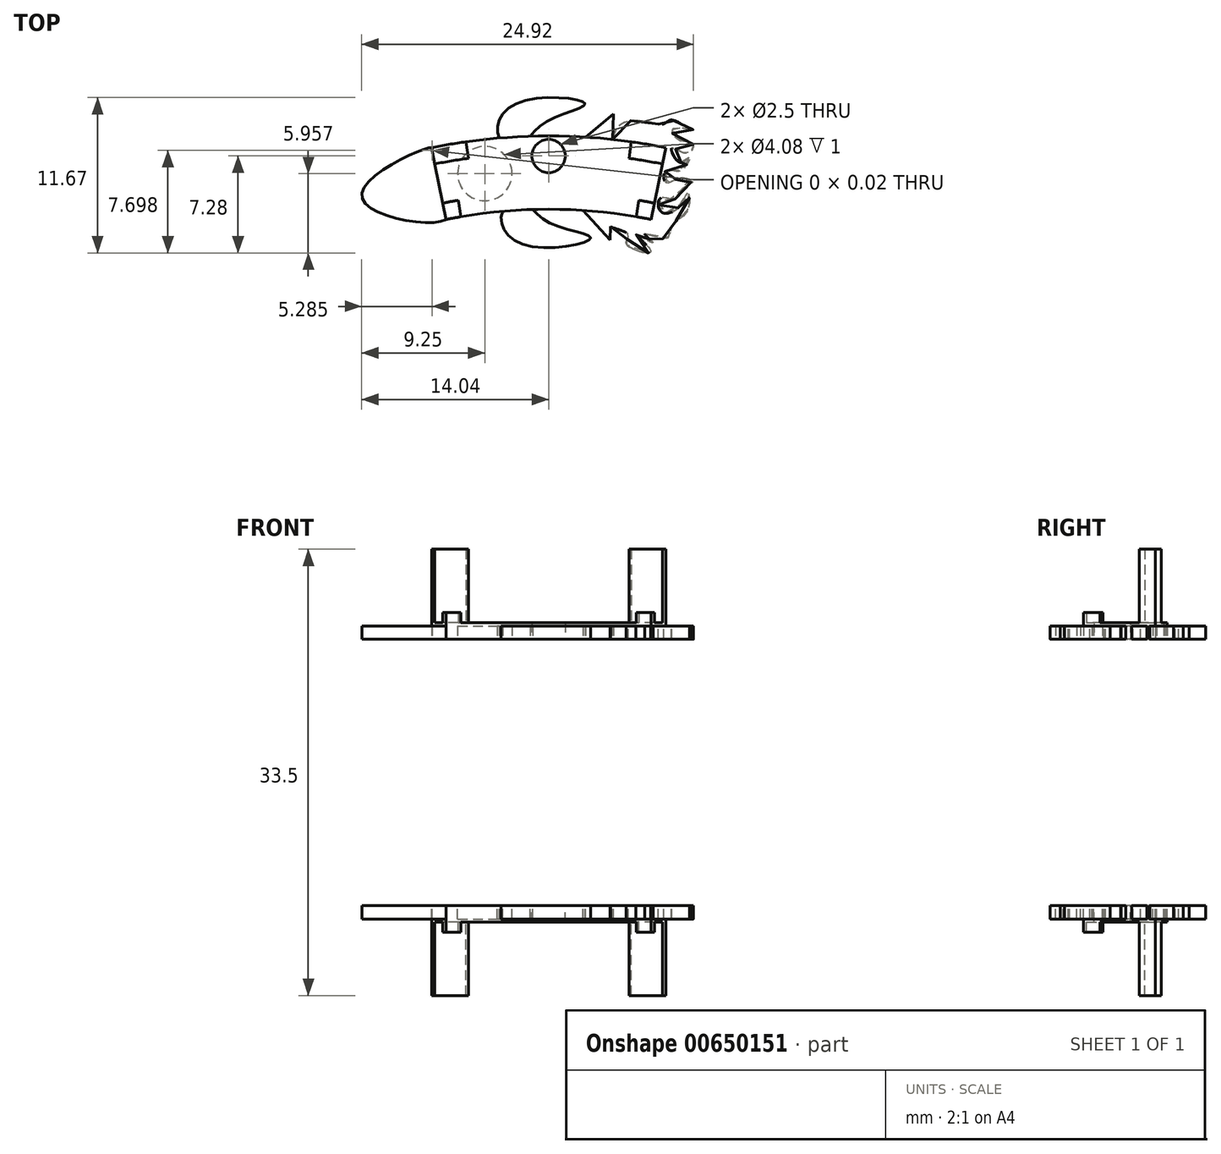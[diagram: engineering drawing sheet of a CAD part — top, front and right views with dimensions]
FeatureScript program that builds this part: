
annotation { "Feature Type Name" : "Feature", "Feature Type Description" : "" }
export const myFeature = defineFeature(function(context is Context, id is Id, definition is map)
    precondition{}
    {
        {
            var Q0;
            Q0=qCreatedBy(makeId("Top.planeOp"),FACE);
            var sketch = newSketch(context, id + "F0", { "sketchPlane" : qUnion([Q0])});
            skCircle(sketch, "E0", {"center": v(0, 0) * mm, "radius": 39 * mm});
            skCircle(sketch, "E1", {"center": v(0, 0) * mm, "radius": 44.5 * mm});
            skCircle(sketch, "E2", {"center": v(0, 43) * mm, "radius": 1.25 * mm});
            skCircle(sketch, "E3", {"center": v(0, 43) * mm, "radius": 6 * mm});
            skLineSegment(sketch, "E4", {"start": v(-7.7, 38.23) * mm, "end": v(-8.8, 43.62) * mm});
            skLineSegment(sketch, "E5", {"start": v(7.7, 38.23) * mm, "end": v(8.8, 43.62) * mm});
            skLineSegment(sketch, "E6", {"start": v(-7.5, 43.86) * mm, "end": v(-6.58, 38.44) * mm});
            skLineSegment(sketch, "E7", {"start": v(6.58, 38.44) * mm, "end": v(7.5, 43.86) * mm});
            skCircle(sketch, "E8", {"center": v(0, 0) * mm, "radius": 40.25 * mm});
            skCircle(sketch, "E9", {"center": v(0, 0) * mm, "radius": 43.25 * mm});
            skSolve(sketch);
        }
        {
            var Q0;
            {var subQ0=sQuery(id+"F0.wireOp",EDGE,"E7");var subQ1=sQuery(id+"F0.wireOp",EDGE,"E1");var subQ2=makeQuery(id+"F0.imprint","INTERSECT",VERTEX,{"derivedFrom":[subQ1,subQ0]});Q0=makeQuery(id+"F0.imprint","IMPRINT",FACE,{"disambiguationData":[TD([[makeQuery(id+"F0.imprint","IMPRINT",EDGE,{"disambiguationData":[TD([[subQ2,-1.0]])],"derivedFrom":subQ1}),1.0]])]});}
            var Q1;
            {var subQ0=sQuery(id+"F0.wireOp",EDGE,"E6");var subQ1=sQuery(id+"F0.wireOp",EDGE,"E1");var subQ2=makeQuery(id+"F0.imprint","INTERSECT",VERTEX,{"derivedFrom":[subQ1,subQ0]});Q1=makeQuery(id+"F0.imprint","IMPRINT",FACE,{"disambiguationData":[TD([[makeQuery(id+"F0.imprint","IMPRINT",EDGE,{"disambiguationData":[TD([[subQ2,1.0]])],"derivedFrom":subQ1}),1.0]])]});}
            var Q2;
            {var subQ0=sQuery(id+"F0.wireOp",EDGE,"E3");var subQ1=sQuery(id+"F0.wireOp",EDGE,"E1");var subQ2=makeQuery(id+"F0.imprint","INTERSECT",VERTEX,{"disambiguationData":[OD(0.0)],"derivedFrom":[subQ1,subQ0]});Q2=makeQuery(id+"F0.imprint","IMPRINT",FACE,{"disambiguationData":[TD([[makeQuery(id+"F0.imprint","IMPRINT",EDGE,{"disambiguationData":[TD([[subQ2,-1.0]])],"derivedFrom":subQ1}),1.0]])]});}
            var Q3;
            {var subQ0=sQuery(id+"F0.wireOp",EDGE,"E8");var subQ1=sQuery(id+"F0.wireOp",EDGE,"E3");var subQ2=makeQuery(id+"F0.imprint","INTERSECT",VERTEX,{"disambiguationData":[OD(1.0)],"derivedFrom":[subQ1,subQ0]});Q3=makeQuery(id+"F0.imprint","IMPRINT",FACE,{"disambiguationData":[TD([[makeQuery(id+"F0.imprint","IMPRINT",EDGE,{"disambiguationData":[TD([[subQ2,-1.0]])],"derivedFrom":subQ1}),-1.0]])]});}
            var Q4;
            {var subQ3=sQuery(id+"F0.wireOp",EDGE,"E9");var subQ5=sQuery(id+"F0.wireOp",EDGE,"E2");var subQ6=makeQuery(id+"F0.imprint","INTERSECT",VERTEX,{"disambiguationData":[OD(0.0)],"derivedFrom":[subQ5,subQ3]});Q4=makeQuery(id+"F0.imprint","IMPRINT",FACE,{"disambiguationData":[TD([[makeQuery(id+"F0.imprint","IMPRINT",EDGE,{"disambiguationData":[TD([[subQ6,1.0]])],"derivedFrom":subQ5}),-1.0]])]});}
            var Q5;
            {var subQ0=sQuery(id+"F0.wireOp",EDGE,"E9");var subQ1=sQuery(id+"F0.wireOp",EDGE,"E3");var subQ2=makeQuery(id+"F0.imprint","INTERSECT",VERTEX,{"disambiguationData":[OD(0.0)],"derivedFrom":[subQ1,subQ0]});Q5=makeQuery(id+"F0.imprint","IMPRINT",FACE,{"disambiguationData":[TD([[makeQuery(id+"F0.imprint","IMPRINT",EDGE,{"disambiguationData":[TD([[subQ2,-1.0]])],"derivedFrom":subQ1}),-1.0]])]});}
            var Q6;
            {var subQ0=sQuery(id+"F0.wireOp",EDGE,"E6");var subQ1=sQuery(id+"F0.wireOp",EDGE,"E0");var subQ2=makeQuery(id+"F0.imprint","INTERSECT",VERTEX,{"derivedFrom":[subQ1,subQ0]});Q6=makeQuery(id+"F0.imprint","IMPRINT",FACE,{"disambiguationData":[TD([[makeQuery(id+"F0.imprint","IMPRINT",EDGE,{"disambiguationData":[TD([[subQ2,1.0]])],"derivedFrom":subQ1}),-1.0]])]});}
            var Q7;
            {var subQ0=sQuery(id+"F0.wireOp",EDGE,"E3");var subQ1=sQuery(id+"F0.wireOp",EDGE,"E0");var subQ2=makeQuery(id+"F0.imprint","INTERSECT",VERTEX,{"disambiguationData":[OD(0.0)],"derivedFrom":[subQ1,subQ0]});Q7=makeQuery(id+"F0.imprint","IMPRINT",FACE,{"disambiguationData":[TD([[makeQuery(id+"F0.imprint","IMPRINT",EDGE,{"disambiguationData":[TD([[subQ2,-1.0]])],"derivedFrom":subQ1}),-1.0]])]});}
            var Q8;
            {var subQ0=sQuery(id+"F0.wireOp",EDGE,"E7");var subQ1=sQuery(id+"F0.wireOp",EDGE,"E0");var subQ2=makeQuery(id+"F0.imprint","INTERSECT",VERTEX,{"derivedFrom":[subQ1,subQ0]});Q8=makeQuery(id+"F0.imprint","IMPRINT",FACE,{"disambiguationData":[TD([[makeQuery(id+"F0.imprint","IMPRINT",EDGE,{"disambiguationData":[TD([[subQ2,-1.0]])],"derivedFrom":subQ1}),-1.0]])]});}
            var Q9;
            {var subQ0=sQuery(id+"F0.wireOp",EDGE,"E8");var subQ1=sQuery(id+"F0.wireOp",EDGE,"E5");var subQ2=makeQuery(id+"F0.imprint","INTERSECT",VERTEX,{"derivedFrom":[subQ1,subQ0]});Q9=makeQuery(id+"F0.imprint","IMPRINT",FACE,{"disambiguationData":[TD([[makeQuery(id+"F0.imprint","IMPRINT",EDGE,{"disambiguationData":[TD([[subQ2,-1.0]])],"derivedFrom":subQ1}),1.0]])]});}
            var Q10;
            {var subQ0=sQuery(id+"F0.wireOp",EDGE,"E8");var subQ1=sQuery(id+"F0.wireOp",EDGE,"E4");var subQ2=makeQuery(id+"F0.imprint","INTERSECT",VERTEX,{"derivedFrom":[subQ1,subQ0]});Q10=makeQuery(id+"F0.imprint","IMPRINT",FACE,{"disambiguationData":[TD([[makeQuery(id+"F0.imprint","IMPRINT",EDGE,{"disambiguationData":[TD([[subQ2,-1.0]])],"derivedFrom":subQ1}),-1.0]])]});}
            extrude(context, id + "F1", {"entities" : qUnion([Q0, Q1, Q2, Q3, Q4, Q5, Q6, Q7, Q8, Q9, Q10]), "depth" : 1.25 * mm, "offsetDistance" : 25 * mm});
        }
        {
            var Q0;
            Q0=qCreatedBy(makeId("Top.planeOp"),FACE);
            var sketch = newSketch(context, id + "F2", { "sketchPlane" : qUnion([Q0])});
            skCircle(sketch, "E10", {"center": v(0, 0) * mm, "radius": 39 * mm});
            skCircle(sketch, "E11", {"center": v(0, 0) * mm, "radius": 44.5 * mm});
            skCircle(sketch, "E12", {"center": v(0, 43) * mm, "radius": 0.85 * mm});
            skCircle(sketch, "E13", {"center": v(0, 43) * mm, "radius": 6 * mm});
            skLineSegment(sketch, "E14", {"start": v(-7.7, 38.23) * mm, "end": v(-8.8, 43.62) * mm});
            skLineSegment(sketch, "E15", {"start": v(7.7, 38.23) * mm, "end": v(8.8, 43.62) * mm});
            skLineSegment(sketch, "E16", {"start": v(-6.2, 44.06) * mm, "end": v(-5.44, 38.62) * mm});
            skLineSegment(sketch, "E17", {"start": v(5.44, 38.62) * mm, "end": v(6.2, 44.06) * mm});
            skCircle(sketch, "E18", {"center": v(0, 0) * mm, "radius": 40.25 * mm});
            skCircle(sketch, "E19", {"center": v(0, 0) * mm, "radius": 43.25 * mm});
            skSolve(sketch);
        }
        {
            var Q0;
            {var subQ0=sQuery(id+"F2.wireOp",EDGE,"E15");var subQ1=sQuery(id+"F2.wireOp",EDGE,"E11");var subQ2=makeQuery(id+"F2.imprint","INTERSECT",VERTEX,{"derivedFrom":[subQ1,subQ0]});Q0=makeQuery(id+"F2.imprint","IMPRINT",FACE,{"disambiguationData":[TD([[makeQuery(id+"F2.imprint","IMPRINT",EDGE,{"disambiguationData":[TD([[subQ2,-1.0]])],"derivedFrom":subQ1}),1.0]])]});}
            var Q1;
            {var subQ0=sQuery(id+"F2.wireOp",EDGE,"E14");var subQ1=sQuery(id+"F2.wireOp",EDGE,"E11");var subQ2=makeQuery(id+"F2.imprint","INTERSECT",VERTEX,{"derivedFrom":[subQ1,subQ0]});Q1=makeQuery(id+"F2.imprint","IMPRINT",FACE,{"disambiguationData":[TD([[makeQuery(id+"F2.imprint","IMPRINT",EDGE,{"disambiguationData":[TD([[subQ2,1.0]])],"derivedFrom":subQ1}),1.0]])]});}
            extrude(context, id + "F3", {"entities" : qUnion([Q0, Q1]), "operationType" : NewBodyOperationType.ADD, "depth" : 6.75 * mm, "offsetDistance" : 25 * mm});
        }
        {
            var Q0;
            Q0=qCreatedBy(makeId("Top.planeOp"),FACE);
            var sketch = newSketch(context, id + "F4", { "sketchPlane" : qUnion([Q0])});
            skCircle(sketch, "E20", {"center": v(0, 0) * mm, "radius": 39 * mm});
            skCircle(sketch, "E21", {"center": v(0, 0) * mm, "radius": 44.5 * mm});
            skCircle(sketch, "E22", {"center": v(0, 43) * mm, "radius": 0.85 * mm});
            skCircle(sketch, "E23", {"center": v(0, 43) * mm, "radius": 6 * mm});
            skLineSegment(sketch, "E24", {"start": v(-7.7, 38.23) * mm, "end": v(-8.8, 43.62) * mm});
            skLineSegment(sketch, "E25", {"start": v(7.7, 38.23) * mm, "end": v(8.8, 43.62) * mm});
            skLineSegment(sketch, "E26", {"start": v(-7.5, 43.86) * mm, "end": v(-6.58, 38.44) * mm});
            skLineSegment(sketch, "E27", {"start": v(6.58, 38.44) * mm, "end": v(7.5, 43.86) * mm});
            skCircle(sketch, "E28", {"center": v(0, 0) * mm, "radius": 40.25 * mm});
            skCircle(sketch, "E29", {"center": v(0, 0) * mm, "radius": 43.25 * mm});
            skSolve(sketch);
        }
        {
            var Q0;
            {var subQ0=sQuery(id+"F4.wireOp",EDGE,"E24");var subQ1=sQuery(id+"F4.wireOp",EDGE,"E20");var subQ2=makeQuery(id+"F4.imprint","INTERSECT",VERTEX,{"derivedFrom":[subQ1,subQ0]});Q0=makeQuery(id+"F4.imprint","IMPRINT",FACE,{"disambiguationData":[TD([[makeQuery(id+"F4.imprint","IMPRINT",EDGE,{"disambiguationData":[TD([[subQ2,1.0]])],"derivedFrom":subQ1}),-1.0]])]});}
            var Q1;
            {var subQ0=sQuery(id+"F4.wireOp",EDGE,"E25");var subQ1=sQuery(id+"F4.wireOp",EDGE,"E20");var subQ2=makeQuery(id+"F4.imprint","INTERSECT",VERTEX,{"derivedFrom":[subQ1,subQ0]});Q1=makeQuery(id+"F4.imprint","IMPRINT",FACE,{"disambiguationData":[TD([[makeQuery(id+"F4.imprint","IMPRINT",EDGE,{"disambiguationData":[TD([[subQ2,-1.0]])],"derivedFrom":subQ1}),-1.0]])]});}
            extrude(context, id + "F5", {"entities" : qUnion([Q0, Q1]), "operationType" : NewBodyOperationType.ADD, "depth" : 2 * mm, "offsetDistance" : 25 * mm});
        }
        {
            var Q0;
            {var subQ0=sQuery(id+"F4.wireOp",EDGE,"E28");var subQ1=sQuery(id+"F4.wireOp",EDGE,"E20");var subQ2=sQuery(id+"F2.wireOp",EDGE,"E19");var subQ3=sQuery(id+"F2.wireOp",EDGE,"E11");Q0=makeQuery(id+"F5.boolean.opBoolean","MERGE",FACE,{"derivedFrom":[makeQuery(id+"F3.boolean.opBoolean","MERGE",FACE,{"derivedFrom":[makeQuery(id+"F1.opExtrude","CAP_FACE",FACE,{"disambiguationData":[OSD([sQuery(id+"F0.wireOp",EDGE,"E0"),sQuery(id+"F0.wireOp",EDGE,"E1"),sQuery(id+"F0.wireOp",EDGE,"E2"),sQuery(id+"F0.wireOp",EDGE,"E4"),sQuery(id+"F0.wireOp",EDGE,"E5"),sQuery(id+"F0.wireOp",EDGE,"E6"),sQuery(id+"F0.wireOp",EDGE,"E7"),sQuery(id+"F0.wireOp",EDGE,"E8"),sQuery(id+"F0.wireOp",EDGE,"E9")])],"isStart":true}),makeQuery(id+"F3.opExtrude","CAP_FACE",FACE,{"disambiguationData":[OSD([subQ3,sQuery(id+"F2.wireOp",EDGE,"E15"),sQuery(id+"F2.wireOp",EDGE,"E17"),subQ2])],"isStart":true}),makeQuery(id+"F3.opExtrude","CAP_FACE",FACE,{"disambiguationData":[OSD([subQ3,sQuery(id+"F2.wireOp",EDGE,"E14"),sQuery(id+"F2.wireOp",EDGE,"E16"),subQ2])],"isStart":true})]}),makeQuery(id+"F5.opExtrude","CAP_FACE",FACE,{"disambiguationData":[OSD([subQ1,sQuery(id+"F4.wireOp",EDGE,"E25"),sQuery(id+"F4.wireOp",EDGE,"E27"),subQ0])],"isStart":true}),makeQuery(id+"F5.opExtrude","CAP_FACE",FACE,{"disambiguationData":[OSD([subQ1,sQuery(id+"F4.wireOp",EDGE,"E24"),sQuery(id+"F4.wireOp",EDGE,"E26"),subQ0])],"isStart":true})]});}
            var sketch = newSketch(context, id + "F6", { "sketchPlane" : qUnion([Q0])});
            skFitSpline(sketch, "E30", {"points": [v(-8.8, -43.62) * mm, v(-14.04, -40.05) * mm, v(-7.7, -38.23) * mm, v(-7.7, -39.96) * mm, v(-8, -41.27) * mm, v(-8.21, -42.6) * mm, v(-8.43, -43.18) * mm, v(-8.75, -43.41) * mm, v(-8.8, -43.62) * mm]});
            skSolve(sketch);
        }
        {
            var Q0;
            Q0=qSketchRegion(id+"F6",true);
            extrude(context, id + "F7", {"entities" : qUnion([Q0]), "operationType" : NewBodyOperationType.ADD, "oppositeDirection" : true, "depth" : 1 * mm, "offsetDistance" : 25 * mm});
        }
        {
            var Q0;
            {var subQ0=sQuery(id+"F4.wireOp",EDGE,"E28");var subQ1=sQuery(id+"F4.wireOp",EDGE,"E20");var subQ2=sQuery(id+"F2.wireOp",EDGE,"E19");var subQ3=sQuery(id+"F2.wireOp",EDGE,"E11");Q0=makeQuery(id+"F7.boolean.opBoolean","MERGE",FACE,{"derivedFrom":[makeQuery(id+"F5.boolean.opBoolean","MERGE",FACE,{"derivedFrom":[makeQuery(id+"F3.boolean.opBoolean","MERGE",FACE,{"derivedFrom":[makeQuery(id+"F1.opExtrude","CAP_FACE",FACE,{"disambiguationData":[OSD([sQuery(id+"F0.wireOp",EDGE,"E0"),sQuery(id+"F0.wireOp",EDGE,"E1"),sQuery(id+"F0.wireOp",EDGE,"E2"),sQuery(id+"F0.wireOp",EDGE,"E4"),sQuery(id+"F0.wireOp",EDGE,"E5"),sQuery(id+"F0.wireOp",EDGE,"E6"),sQuery(id+"F0.wireOp",EDGE,"E7"),sQuery(id+"F0.wireOp",EDGE,"E8"),sQuery(id+"F0.wireOp",EDGE,"E9")])],"isStart":true}),makeQuery(id+"F3.opExtrude","CAP_FACE",FACE,{"disambiguationData":[OSD([subQ3,sQuery(id+"F2.wireOp",EDGE,"E15"),sQuery(id+"F2.wireOp",EDGE,"E17"),subQ2])],"isStart":true}),makeQuery(id+"F3.opExtrude","CAP_FACE",FACE,{"disambiguationData":[OSD([subQ3,sQuery(id+"F2.wireOp",EDGE,"E14"),sQuery(id+"F2.wireOp",EDGE,"E16"),subQ2])],"isStart":true})]}),makeQuery(id+"F5.opExtrude","CAP_FACE",FACE,{"disambiguationData":[OSD([subQ1,sQuery(id+"F4.wireOp",EDGE,"E25"),sQuery(id+"F4.wireOp",EDGE,"E27"),subQ0])],"isStart":true}),makeQuery(id+"F5.opExtrude","CAP_FACE",FACE,{"disambiguationData":[OSD([subQ1,sQuery(id+"F4.wireOp",EDGE,"E24"),sQuery(id+"F4.wireOp",EDGE,"E26"),subQ0])],"isStart":true})]}),makeQuery(id+"F7.opExtrude","CAP_FACE",FACE,{"disambiguationData":[OSD([sQuery(id+"F6.wireOp",EDGE,"E30")])],"isStart":true})]});}
            var sketch = newSketch(context, id + "F8", { "sketchPlane" : qUnion([Q0])});
            skCircle(sketch, "E31", {"center": v(-4.8, -41.68) * mm, "radius": 2.04 * mm});
            skSolve(sketch);
        }
        {
            var Q0;
            Q0=qSketchRegion(id+"F8",true);
            extrude(context, id + "F9", {"entities" : qUnion([Q0]), "operationType" : NewBodyOperationType.REMOVE, "oppositeDirection" : true, "depth" : 1 * mm, "offsetDistance" : 25 * mm});
        }
        {
            var Q0;
            {var subQ0=sQuery(id+"F4.wireOp",EDGE,"E28");var subQ1=sQuery(id+"F4.wireOp",EDGE,"E20");var subQ2=sQuery(id+"F2.wireOp",EDGE,"E19");var subQ3=sQuery(id+"F2.wireOp",EDGE,"E11");Q0=makeQuery(id+"F7.boolean.opBoolean","MERGE",FACE,{"derivedFrom":[makeQuery(id+"F5.boolean.opBoolean","MERGE",FACE,{"derivedFrom":[makeQuery(id+"F3.boolean.opBoolean","MERGE",FACE,{"derivedFrom":[makeQuery(id+"F1.opExtrude","CAP_FACE",FACE,{"disambiguationData":[OSD([sQuery(id+"F0.wireOp",EDGE,"E0"),sQuery(id+"F0.wireOp",EDGE,"E1"),sQuery(id+"F0.wireOp",EDGE,"E2"),sQuery(id+"F0.wireOp",EDGE,"E4"),sQuery(id+"F0.wireOp",EDGE,"E5"),sQuery(id+"F0.wireOp",EDGE,"E6"),sQuery(id+"F0.wireOp",EDGE,"E7"),sQuery(id+"F0.wireOp",EDGE,"E8"),sQuery(id+"F0.wireOp",EDGE,"E9")])],"isStart":true}),makeQuery(id+"F3.opExtrude","CAP_FACE",FACE,{"disambiguationData":[OSD([subQ3,sQuery(id+"F2.wireOp",EDGE,"E15"),sQuery(id+"F2.wireOp",EDGE,"E17"),subQ2])],"isStart":true}),makeQuery(id+"F3.opExtrude","CAP_FACE",FACE,{"disambiguationData":[OSD([subQ3,sQuery(id+"F2.wireOp",EDGE,"E14"),sQuery(id+"F2.wireOp",EDGE,"E16"),subQ2])],"isStart":true})]}),makeQuery(id+"F5.opExtrude","CAP_FACE",FACE,{"disambiguationData":[OSD([subQ1,sQuery(id+"F4.wireOp",EDGE,"E25"),sQuery(id+"F4.wireOp",EDGE,"E27"),subQ0])],"isStart":true}),makeQuery(id+"F5.opExtrude","CAP_FACE",FACE,{"disambiguationData":[OSD([subQ1,sQuery(id+"F4.wireOp",EDGE,"E24"),sQuery(id+"F4.wireOp",EDGE,"E26"),subQ0])],"isStart":true})]}),makeQuery(id+"F7.opExtrude","CAP_FACE",FACE,{"disambiguationData":[OSD([sQuery(id+"F6.wireOp",EDGE,"E30")])],"isStart":true})]});}
            var sketch = newSketch(context, id + "F10", { "sketchPlane" : qUnion([Q0])});
            skFitSpline(sketch, "E32", {"points": [v(-2.2, -43.63) * mm, v(-3.7, -44.35) * mm, v(-2.48, -46.91) * mm, v(2.73, -46.92) * mm, v(-0.49, -45.38) * mm, v(-2.2, -43.63) * mm]});
            skLineSegment(sketch, "E33", {"start": v(3.58, -41.9) * mm, "end": v(-9.05, -41.36) * mm});
            skFitSpline(sketch, "E34.MirrorC", {"points": [v(-2.03, -39.69) * mm, v(-3.46, -38.84) * mm, v(-2.03, -36.4) * mm, v(3.16, -36.83) * mm, v(-0.17, -38.1) * mm, v(-2.03, -39.69) * mm]});
            skSolve(sketch);
        }
        {
            var Q0;
            Q0=qSketchRegion(id+"F10",true);
            extrude(context, id + "F11", {"entities" : qUnion([Q0]), "operationType" : NewBodyOperationType.ADD, "oppositeDirection" : true, "depth" : 1 * mm, "offsetDistance" : 25 * mm});
        }
        {
            var Q0;
            {var subQ0=sQuery(id+"F4.wireOp",EDGE,"E28");var subQ1=sQuery(id+"F4.wireOp",EDGE,"E20");var subQ2=sQuery(id+"F2.wireOp",EDGE,"E19");var subQ3=sQuery(id+"F2.wireOp",EDGE,"E11");Q0=makeQuery(id+"F11.boolean.opBoolean","MERGE",FACE,{"derivedFrom":[makeQuery(id+"F7.boolean.opBoolean","MERGE",FACE,{"derivedFrom":[makeQuery(id+"F5.boolean.opBoolean","MERGE",FACE,{"derivedFrom":[makeQuery(id+"F3.boolean.opBoolean","MERGE",FACE,{"derivedFrom":[makeQuery(id+"F1.opExtrude","CAP_FACE",FACE,{"disambiguationData":[OSD([sQuery(id+"F0.wireOp",EDGE,"E0"),sQuery(id+"F0.wireOp",EDGE,"E1"),sQuery(id+"F0.wireOp",EDGE,"E2"),sQuery(id+"F0.wireOp",EDGE,"E4"),sQuery(id+"F0.wireOp",EDGE,"E5"),sQuery(id+"F0.wireOp",EDGE,"E6"),sQuery(id+"F0.wireOp",EDGE,"E7"),sQuery(id+"F0.wireOp",EDGE,"E8"),sQuery(id+"F0.wireOp",EDGE,"E9")])],"isStart":true}),makeQuery(id+"F3.opExtrude","CAP_FACE",FACE,{"disambiguationData":[OSD([subQ3,sQuery(id+"F2.wireOp",EDGE,"E15"),sQuery(id+"F2.wireOp",EDGE,"E17"),subQ2])],"isStart":true}),makeQuery(id+"F3.opExtrude","CAP_FACE",FACE,{"disambiguationData":[OSD([subQ3,sQuery(id+"F2.wireOp",EDGE,"E14"),sQuery(id+"F2.wireOp",EDGE,"E16"),subQ2])],"isStart":true})]}),makeQuery(id+"F5.opExtrude","CAP_FACE",FACE,{"disambiguationData":[OSD([subQ1,sQuery(id+"F4.wireOp",EDGE,"E25"),sQuery(id+"F4.wireOp",EDGE,"E27"),subQ0])],"isStart":true}),makeQuery(id+"F5.opExtrude","CAP_FACE",FACE,{"disambiguationData":[OSD([subQ1,sQuery(id+"F4.wireOp",EDGE,"E24"),sQuery(id+"F4.wireOp",EDGE,"E26"),subQ0])],"isStart":true})]}),makeQuery(id+"F7.opExtrude","CAP_FACE",FACE,{"disambiguationData":[OSD([sQuery(id+"F6.wireOp",EDGE,"E30")])],"isStart":true})]}),makeQuery(id+"F11.opExtrude","CAP_FACE",FACE,{"disambiguationData":[OSD([sQuery(id+"F10.wireOp",EDGE,"E32")])],"isStart":true}),makeQuery(id+"F11.opExtrude","CAP_FACE",FACE,{"disambiguationData":[OSD([sQuery(id+"F10.wireOp",EDGE,"E34.MirrorC")])],"isStart":true})]});}
            var sketch = newSketch(context, id + "F12", { "sketchPlane" : qUnion([Q0])});
            skLineSegment(sketch, "E35", {"start": v(2.76, -44.41) * mm, "end": v(4.86, -46.16) * mm});
            skLineSegment(sketch, "E36", {"start": v(4.86, -46.16) * mm, "end": v(4.62, -36.7) * mm});
            skLineSegment(sketch, "E37", {"start": v(4.62, -36.7) * mm, "end": v(2.6, -38.91) * mm});
            skLineSegment(sketch, "E38", {"start": v(2.6, -38.91) * mm, "end": v(2.76, -44.41) * mm});
            skSolve(sketch);
        }
        {
            var Q0;
            Q0=qSketchRegion(id+"F12",true);
            extrude(context, id + "F13", {"entities" : qUnion([Q0]), "operationType" : NewBodyOperationType.ADD, "oppositeDirection" : true, "depth" : 1 * mm, "offsetDistance" : 25 * mm});
        }
        {
            var Q0;
            {var subQ0=sQuery(id+"F4.wireOp",EDGE,"E28");var subQ1=sQuery(id+"F4.wireOp",EDGE,"E20");var subQ2=sQuery(id+"F2.wireOp",EDGE,"E19");var subQ3=sQuery(id+"F2.wireOp",EDGE,"E11");Q0=makeQuery(id+"F13.boolean.opBoolean","MERGE",FACE,{"derivedFrom":[makeQuery(id+"F11.boolean.opBoolean","MERGE",FACE,{"derivedFrom":[makeQuery(id+"F7.boolean.opBoolean","MERGE",FACE,{"derivedFrom":[makeQuery(id+"F5.boolean.opBoolean","MERGE",FACE,{"derivedFrom":[makeQuery(id+"F3.boolean.opBoolean","MERGE",FACE,{"derivedFrom":[makeQuery(id+"F1.opExtrude","CAP_FACE",FACE,{"disambiguationData":[OSD([sQuery(id+"F0.wireOp",EDGE,"E0"),sQuery(id+"F0.wireOp",EDGE,"E1"),sQuery(id+"F0.wireOp",EDGE,"E2"),sQuery(id+"F0.wireOp",EDGE,"E4"),sQuery(id+"F0.wireOp",EDGE,"E5"),sQuery(id+"F0.wireOp",EDGE,"E6"),sQuery(id+"F0.wireOp",EDGE,"E7"),sQuery(id+"F0.wireOp",EDGE,"E8"),sQuery(id+"F0.wireOp",EDGE,"E9")])],"isStart":true}),makeQuery(id+"F3.opExtrude","CAP_FACE",FACE,{"disambiguationData":[OSD([subQ3,sQuery(id+"F2.wireOp",EDGE,"E15"),sQuery(id+"F2.wireOp",EDGE,"E17"),subQ2])],"isStart":true}),makeQuery(id+"F3.opExtrude","CAP_FACE",FACE,{"disambiguationData":[OSD([subQ3,sQuery(id+"F2.wireOp",EDGE,"E14"),sQuery(id+"F2.wireOp",EDGE,"E16"),subQ2])],"isStart":true})]}),makeQuery(id+"F5.opExtrude","CAP_FACE",FACE,{"disambiguationData":[OSD([subQ1,sQuery(id+"F4.wireOp",EDGE,"E25"),sQuery(id+"F4.wireOp",EDGE,"E27"),subQ0])],"isStart":true}),makeQuery(id+"F5.opExtrude","CAP_FACE",FACE,{"disambiguationData":[OSD([subQ1,sQuery(id+"F4.wireOp",EDGE,"E24"),sQuery(id+"F4.wireOp",EDGE,"E26"),subQ0])],"isStart":true})]}),makeQuery(id+"F7.opExtrude","CAP_FACE",FACE,{"disambiguationData":[OSD([sQuery(id+"F6.wireOp",EDGE,"E30")])],"isStart":true})]}),makeQuery(id+"F11.opExtrude","CAP_FACE",FACE,{"disambiguationData":[OSD([sQuery(id+"F10.wireOp",EDGE,"E32")])],"isStart":true}),makeQuery(id+"F11.opExtrude","CAP_FACE",FACE,{"disambiguationData":[OSD([sQuery(id+"F10.wireOp",EDGE,"E34.MirrorC")])],"isStart":true})]}),makeQuery(id+"F13.opExtrude","CAP_FACE",FACE,{"disambiguationData":[OSD([sQuery(id+"F12.wireOp",EDGE,"E35"),sQuery(id+"F12.wireOp",EDGE,"E36"),sQuery(id+"F12.wireOp",EDGE,"E37"),sQuery(id+"F12.wireOp",EDGE,"E38")])],"isStart":true})]});}
            var sketch = newSketch(context, id + "F14", { "sketchPlane" : qUnion([Q0])});
            skFitSpline(sketch, "E39", {"points": [v(4.81, -44.24) * mm, v(5.73, -45.55) * mm, v(7.72, -45.54) * mm, v(8.58, -45.39) * mm, v(9.1, -45.69) * mm, v(9.96, -45.42) * mm, v(10.87, -44.98) * mm, v(9.33, -45.02) * mm, v(9.74, -44.24) * mm, v(10.86, -43.85) * mm, v(10.36, -43.18) * mm, v(9.24, -43.62) * mm, v(9.92, -42.51) * mm, v(10.66, -42.97) * mm, v(9.9, -41.9) * mm, v(8.8, -41.89) * mm, v(8.8, -41) * mm, v(10.07, -41.39) * mm, v(10.82, -41.02) * mm, v(10.4, -41) * mm, v(9.53, -39.78) * mm, v(8.44, -39.85) * mm, v(8.37, -38.9) * mm, v(9.7, -39.06) * mm, v(10.48, -40.22) * mm, v(10.4, -38.8) * mm, v(9.29, -37.83) * mm, v(8.8, -36.78) * mm, v(7.22, -37.15) * mm, v(7.84, -36.46) * mm, v(6.56, -37.09) * mm, v(7.67, -35.83) * mm, v(5.87, -36.34) * mm, v(5.98, -37.07) * mm, v(4.64, -37.71) * mm, v(4.06, -38.97) * mm, v(4.81, -44.24) * mm]});
            skSolve(sketch);
        }
        {
            var Q0;
            Q0=qSketchRegion(id+"F14",true);
            extrude(context, id + "F15", {"entities" : qUnion([Q0]), "operationType" : NewBodyOperationType.ADD, "oppositeDirection" : true, "depth" : 1 * mm, "offsetDistance" : 25 * mm});
        }
        {
            var Q0;
            Q0=makeQuery(id+"F1.opExtrude","SWEPT_BODY",BODY,{"disambiguationData":[OSD([sQuery(id+"F0.wireOp",EDGE,"E0"),sQuery(id+"F0.wireOp",EDGE,"E1"),sQuery(id+"F0.wireOp",EDGE,"E2"),sQuery(id+"F0.wireOp",EDGE,"E4"),sQuery(id+"F0.wireOp",EDGE,"E5"),sQuery(id+"F0.wireOp",EDGE,"E6"),sQuery(id+"F0.wireOp",EDGE,"E7"),sQuery(id+"F0.wireOp",EDGE,"E8"),sQuery(id+"F0.wireOp",EDGE,"E9")])]});
            transform(context, id + "F16", {"entities" : qUnion([Q0]), "transformType" : TransformType.TRANSLATION_3D, "dx" : 0 * mm, "dy" : 0 * mm, "dz" : 10 * mm, "makeCopy" : false});
        }
        {
            var Q0;
            Q0=makeQuery(id+"F1.opExtrude","SWEPT_BODY",BODY,{"disambiguationData":[OSD([sQuery(id+"F0.wireOp",EDGE,"E0"),sQuery(id+"F0.wireOp",EDGE,"E1"),sQuery(id+"F0.wireOp",EDGE,"E2"),sQuery(id+"F0.wireOp",EDGE,"E4"),sQuery(id+"F0.wireOp",EDGE,"E5"),sQuery(id+"F0.wireOp",EDGE,"E6"),sQuery(id+"F0.wireOp",EDGE,"E7"),sQuery(id+"F0.wireOp",EDGE,"E8"),sQuery(id+"F0.wireOp",EDGE,"E9")])]});
            var Q1;
            Q1=makeQuery(id+"FD49sIW0BlIO3Eh_1.opPattern","COPY",BODY,{"derivedFrom":makeQuery(id+"F1.opExtrude","SWEPT_BODY",BODY,{"disambiguationData":[OSD([sQuery(id+"F0.wireOp",EDGE,"E0"),sQuery(id+"F0.wireOp",EDGE,"E1"),sQuery(id+"F0.wireOp",EDGE,"E2"),sQuery(id+"F0.wireOp",EDGE,"E4"),sQuery(id+"F0.wireOp",EDGE,"E5"),sQuery(id+"F0.wireOp",EDGE,"E6"),sQuery(id+"F0.wireOp",EDGE,"E7"),sQuery(id+"F0.wireOp",EDGE,"E8"),sQuery(id+"F0.wireOp",EDGE,"E9")])]}),"instanceName":"1"});
            transform(context, id + "F17", {"entities" : qUnion([Q0, Q1]), "transformType" : TransformType.TRANSLATION_3D, "dx" : 30 * mm, "dy" : 0 * mm, "dz" : -10 * mm, "makeCopy" : false});
        }
        {
            var Q0;
            Q0=makeQuery(id+"F1.opExtrude","SWEPT_BODY",BODY,{"disambiguationData":[OSD([sQuery(id+"F0.wireOp",EDGE,"E0"),sQuery(id+"F0.wireOp",EDGE,"E1"),sQuery(id+"F0.wireOp",EDGE,"E2"),sQuery(id+"F0.wireOp",EDGE,"E4"),sQuery(id+"F0.wireOp",EDGE,"E5"),sQuery(id+"F0.wireOp",EDGE,"E6"),sQuery(id+"F0.wireOp",EDGE,"E7"),sQuery(id+"F0.wireOp",EDGE,"E8"),sQuery(id+"F0.wireOp",EDGE,"E9")])]});
            transform(context, id + "F18", {"entities" : qUnion([Q0]), "transformType" : TransformType.TRANSLATION_3D, "dx" : 0 * mm, "dy" : 0 * mm, "dz" : 10 * mm, "makeCopy" : false});
        }
        {
            var Q0;
            Q0=makeQuery(id+"F1.opExtrude","SWEPT_BODY",BODY,{"disambiguationData":[OSD([sQuery(id+"F0.wireOp",EDGE,"E0"),sQuery(id+"F0.wireOp",EDGE,"E1"),sQuery(id+"F0.wireOp",EDGE,"E2"),sQuery(id+"F0.wireOp",EDGE,"E4"),sQuery(id+"F0.wireOp",EDGE,"E5"),sQuery(id+"F0.wireOp",EDGE,"E6"),sQuery(id+"F0.wireOp",EDGE,"E7"),sQuery(id+"F0.wireOp",EDGE,"E8"),sQuery(id+"F0.wireOp",EDGE,"E9")])]});
            var Q1;
            Q1=qCreatedBy(makeId("Top.planeOp"),FACE);
            mirror(context, id + "F19", {"entities" : qUnion([Q0]), "mirrorPlane" : qUnion([Q1])});
        }
    });
